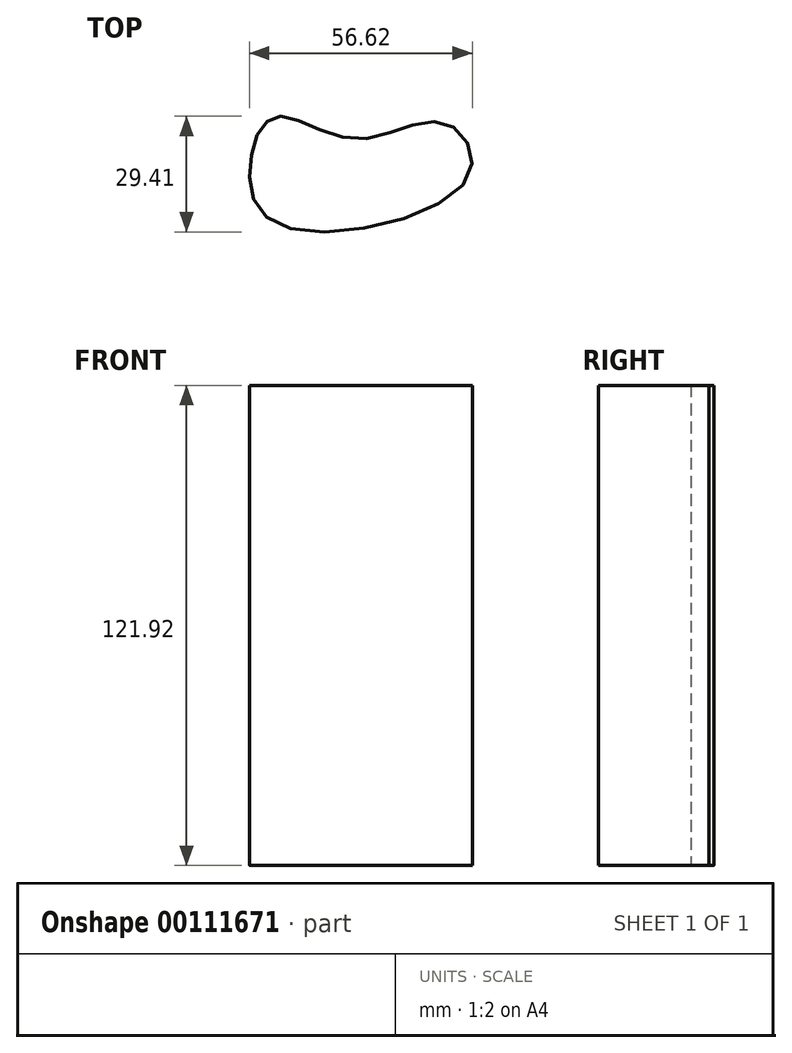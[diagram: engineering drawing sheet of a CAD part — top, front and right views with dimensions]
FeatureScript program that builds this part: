
annotation { "Feature Type Name" : "Feature", "Feature Type Description" : "" }
export const myFeature = defineFeature(function(context is Context, id is Id, definition is map)
    precondition{}
    {
        {
            var Q0;
            Q0=qCreatedBy(makeId("Top.planeOp"),FACE);
            var sketch = newSketch(context, id + "F0", { "sketchPlane" : qUnion([Q0])});
            skFitSpline(sketch, "E0", {"points": [v(-43.16, 42.84) * mm, v(-36.08, 25.08) * mm, v(11.87, 37.06) * mm, v(5.51, 51.07) * mm, v(-16.73, 46.88) * mm, v(-36.37, 52.66) * mm, v(-43.16, 42.84) * mm]});
            skSolve(sketch);
        }
        {
            var Q0;
            Q0=makeQuery(id+"F0.imprint","IMPRINT",FACE,{"disambiguationData":[TD([[makeQuery(id+"F0.imprint","IMPRINT",EDGE,{"derivedFrom":sQuery(id+"F0.wireOp",EDGE,"E0")}),1.0]])]});
            extrude(context, id + "F1", {"entities" : qUnion([Q0]), "depth" : 121.92 * mm});
        }
    });
